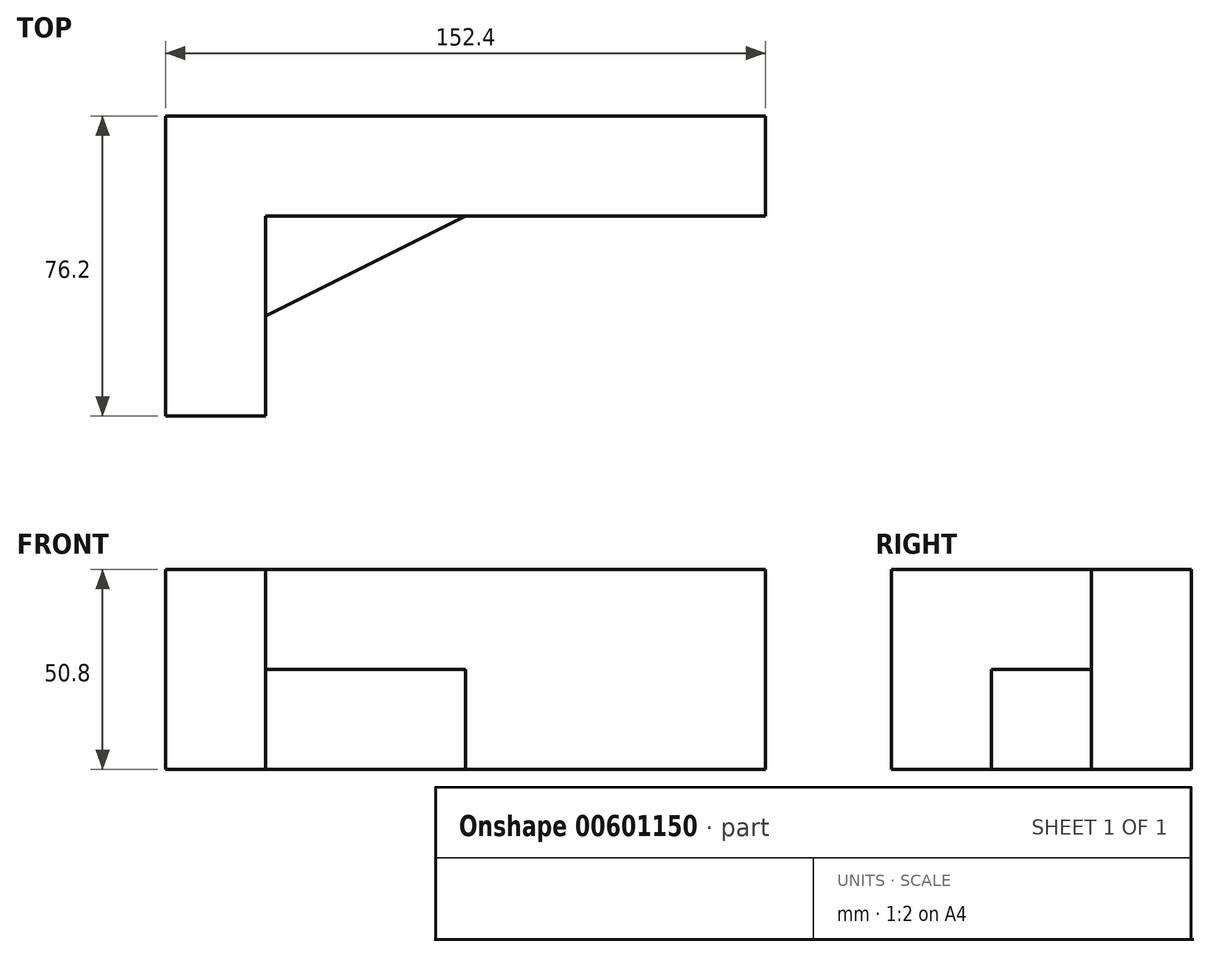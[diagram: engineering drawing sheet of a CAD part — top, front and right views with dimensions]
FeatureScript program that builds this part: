
annotation { "Feature Type Name" : "Feature", "Feature Type Description" : "" }
export const myFeature = defineFeature(function(context is Context, id is Id, definition is map)
    precondition{}
    {
        {
            var Q0;
            Q0=qCreatedBy(makeId("Front.planeOp"),FACE);
            var sketch = newSketch(context, id + "F0", { "sketchPlane" : qUnion([Q0])});
            skLineSegment(sketch, "E0", {"start": v(0, 0) * mm, "end": v(25.4, 0) * mm});
            skLineSegment(sketch, "E1", {"start": v(0, 0) * mm, "end": v(0, 50.8) * mm});
            skLineSegment(sketch, "E2", {"start": v(0, 50.8) * mm, "end": v(152.4, 50.8) * mm});
            skLineSegment(sketch, "E3", {"start": v(152.4, 50.8) * mm, "end": v(152.4, 0) * mm});
            skLineSegment(sketch, "E4", {"start": v(152.4, 0) * mm, "end": v(25.4, 0) * mm});
            skLineSegment(sketch, "E5", {"start": v(25.4, 25.4) * mm, "end": v(76.2, 25.4) * mm});
            skLineSegment(sketch, "E6", {"start": v(76.2, 25.4) * mm, "end": v(76.2, 0) * mm});
            skLineSegment(sketch, "E7", {"start": v(25.4, 0) * mm, "end": v(25.4, 50.8) * mm});
            skSolve(sketch);
        }
        {
            var Q0;
            Q0 = qSketchRegion(id + "F0", true);
            extrude(context, id + "F1", {"entities" : qUnion([Q0]), "oppositeDirection" : true, "depth" : 76.2 * mm, "offsetDistance" : 25.4 * mm});
        }
        {
            var Q0;
            Q0=makeQuery(id+"F1.opExtrude","CAP_FACE",FACE,{"disambiguationData":[OSD([sQuery(id+"F0.wireOp",EDGE,"E0"),sQuery(id+"F0.wireOp",EDGE,"E1"),sQuery(id+"F0.wireOp",EDGE,"E2"),sQuery(id+"F0.wireOp",EDGE,"E3"),sQuery(id+"F0.wireOp",EDGE,"E4")])],"isStart":true});
            var sketch = newSketch(context, id + "F2", { "sketchPlane" : qUnion([Q0])});
            skLineSegment(sketch, "E8", {"start": v(0, 0) * mm, "end": v(25.4, 0) * mm});
            skLineSegment(sketch, "E9", {"start": v(25.4, 0) * mm, "end": v(25.4, 50.8) * mm});
            skLineSegment(sketch, "E10", {"start": v(25.4, 0) * mm, "end": v(76.2, 0) * mm});
            skLineSegment(sketch, "E11", {"start": v(76.2, 0) * mm, "end": v(76.2, 25.4) * mm});
            skLineSegment(sketch, "E12", {"start": v(76.2, 25.4) * mm, "end": v(25.4, 25.4) * mm});
            skLineSegment(sketch, "E13", {"start": v(76.2, 25.4) * mm, "end": v(76.2, 50.8) * mm});
            skSolve(sketch);
        }
        {
            var Q0;
            {var subQ3=sQuery(id+"F2.wireOp",EDGE,"E12");Q0=makeQuery(id+"F2.imprint","IMPRINT",FACE,{"disambiguationData":[TD([[makeQuery(id+"F2.imprint","IMPRINT",EDGE,{"derivedFrom":subQ3}),-1.0]])]});}
            var Q1;
            {var subQ0=sQuery(id+"F2.wireOp",EDGE,"E10");Q1=makeQuery(id+"F2.imprint","IMPRINT",FACE,{"disambiguationData":[TD([[makeQuery(id+"F2.imprint","IMPRINT",EDGE,{"derivedFrom":subQ0}),1.0]])]});}
            extrude(context, id + "F3", {"entities" : qUnion([Q0, Q1]), "operationType" : NewBodyOperationType.REMOVE, "oppositeDirection" : true, "depth" : 25.4 * mm, "offsetDistance" : 25.4 * mm});
        }
        {
            var Q0;
            {var subQ0=sQuery(id+"F0.wireOp",EDGE,"E4");var subQ1=sQuery(id+"F0.wireOp",EDGE,"E0");var subQ2=sQuery(id+"F0.wireOp",EDGE,"E2");var subQ3=sQuery(id+"F0.wireOp",EDGE,"E3");Q0=makeQuery(id+"F3.boolean.opBoolean","SPLIT",FACE,{"disambiguationData":[TD([makeQuery(id+"F1.opExtrude","SWEPT_FACE",FACE,{"disambiguationData":[OSD([subQ3])]})])],"derivedFrom":makeQuery(id+"F1.opExtrude","CAP_FACE",FACE,{"disambiguationData":[OSD([subQ1,sQuery(id+"F0.wireOp",EDGE,"E1"),subQ2,subQ3,subQ0])],"isStart":true})});}
            extrude(context, id + "F4", {"entities" : qUnion([Q0]), "operationType" : NewBodyOperationType.REMOVE, "oppositeDirection" : true, "depth" : 50.8 * mm, "offsetDistance" : 25.4 * mm});
        }
        {
            var Q0;
            Q0=makeQuery(id+"F1.opExtrude","SWEPT_FACE",FACE,{"disambiguationData":[OSD([sQuery(id+"F0.wireOp",EDGE,"E2")])]});
            var sketch = newSketch(context, id + "F5", { "sketchPlane" : qUnion([Q0])});
            skLineSegment(sketch, "E14", {"start": v(25.4, 25.4) * mm, "end": v(76.2, 50.8) * mm});
            skLineSegment(sketch, "E15", {"start": v(76.2, 50.8) * mm, "end": v(25.4, 50.8) * mm});
            skLineSegment(sketch, "E16", {"start": v(25.4, 50.8) * mm, "end": v(25.4, 25.4) * mm});
            skSolve(sketch);
        }
        {
            var Q0;
            Q0=makeQuery(id+"F5.imprint","IMPRINT",FACE,{"disambiguationData":[TD([[makeQuery(id+"F5.imprint","IMPRINT",EDGE,{"derivedFrom":sQuery(id+"F5.wireOp",EDGE,"E14")}),-1.0]])]});
            var Q1;
            Q1=makeQuery(id+"F5.imprint","IMPRINT",FACE,{"disambiguationData":[TD([[makeQuery(id+"F5.imprint","IMPRINT",EDGE,{"derivedFrom":sQuery(id+"F5.wireOp",EDGE,"E14")}),1.0]])]});
            extrude(context, id + "F6", {"entities" : qUnion([Q0, Q1]), "operationType" : NewBodyOperationType.REMOVE, "oppositeDirection" : true, "depth" : 50.8 * mm, "offsetDistance" : 25.4 * mm});
        }
        {
            var Q0;
            Q0=makeQuery(id+"F1.opExtrude","SWEPT_FACE",FACE,{"disambiguationData":[OSD([sQuery(id+"F0.wireOp",EDGE,"E0"),sQuery(id+"F0.wireOp",EDGE,"E4")])]});
            var sketch = newSketch(context, id + "F7", { "sketchPlane" : qUnion([Q0])});
            skLineSegment(sketch, "E17", {"start": v(25.4, -25.4) * mm, "end": v(25.4, -50.8) * mm});
            skLineSegment(sketch, "E18", {"start": v(25.4, -50.8) * mm, "end": v(152.4, -50.8) * mm});
            skLineSegment(sketch, "E19", {"start": v(25.4, -25.4) * mm, "end": v(76.2, -50.8) * mm});
            skSolve(sketch);
        }
        {
            var Q0;
            {var subQ0=sQuery(id+"F7.wireOp",EDGE,"E17");Q0=makeQuery(id+"F7.imprint","IMPRINT",FACE,{"disambiguationData":[TD([[makeQuery(id+"F7.imprint","IMPRINT",EDGE,{"derivedFrom":subQ0}),-1.0]])]});}
            extrude(context, id + "F8", {"entities" : qUnion([Q0]), "operationType" : NewBodyOperationType.ADD, "oppositeDirection" : true, "depth" : 25.4 * mm, "offsetDistance" : 25.4 * mm});
        }
    });
